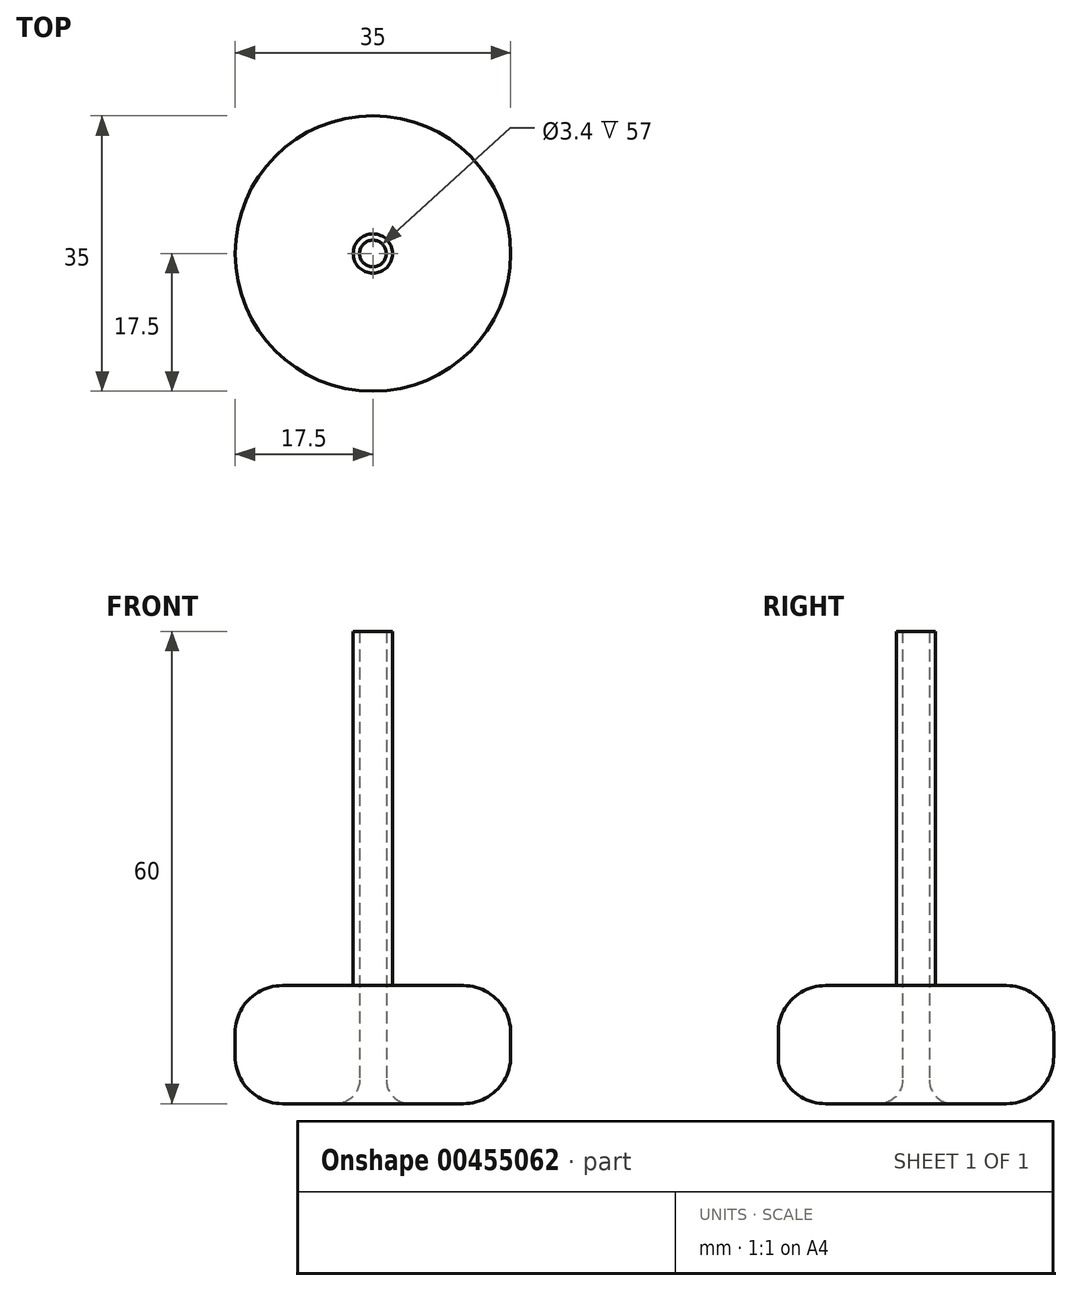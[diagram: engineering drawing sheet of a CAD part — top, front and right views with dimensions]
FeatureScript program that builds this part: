
annotation { "Feature Type Name" : "Feature", "Feature Type Description" : "" }
export const myFeature = defineFeature(function(context is Context, id is Id, definition is map)
    precondition{}
    {
        {
            var Q0;
            Q0=qCreatedBy(makeId("Top.planeOp"),FACE);
            var sketch = newSketch(context, id + "F0", { "sketchPlane" : qUnion([Q0])});
            skCircle(sketch, "E0", {"center": v(0, 0) * mm, "radius": 17.5 * mm});
            skCircle(sketch, "E1", {"center": v(0, 0) * mm, "radius": 2.5 * mm});
            skCircle(sketch, "E2", {"center": v(0, 0) * mm, "radius": 1.7 * mm});
            skSolve(sketch);
        }
        {
            var Q0;
            Q0=makeQuery(id+"F0.imprint","IMPRINT",FACE,{"disambiguationData":[TD([[makeQuery(id+"F0.imprint","IMPRINT",EDGE,{"derivedFrom":sQuery(id+"F0.wireOp",EDGE,"E0")}),1.0]])]});
            extrude(context, id + "F1", {"entities" : qUnion([Q0]), "depth" : 15 * mm});
        }
        {
            var Q0;
            Q0=makeQuery(id+"F1.opExtrude","CAP_EDGE",EDGE,{"disambiguationData":[OSD([sQuery(id+"F0.wireOp",EDGE,"E0")])],"isStart":false});
            var Q1;
            Q1=makeQuery(id+"F1.opExtrude","CAP_EDGE",EDGE,{"disambiguationData":[OSD([sQuery(id+"F0.wireOp",EDGE,"E0")])],"isStart":true});
            fillet(context, id + "F2", {"entities" : qUnion([Q0, Q1]), "radius" : 6 * mm, "tangentPropagation" : true, "allowEdgeOverflow" : false});
        }
        {
            var Q0;
            Q0=makeQuery(id+"F0.imprint","IMPRINT",FACE,{"disambiguationData":[TD([[makeQuery(id+"F0.imprint","IMPRINT",EDGE,{"derivedFrom":sQuery(id+"F0.wireOp",EDGE,"E1")}),1.0]])]});
            extrude(context, id + "F3", {"entities" : qUnion([Q0]), "operationType" : NewBodyOperationType.ADD, "depth" : 60 * mm});
        }
        {
            var Q0;
            Q0=makeQuery(id+"F3.opExtrude","CAP_EDGE",EDGE,{"disambiguationData":[OSD([sQuery(id+"F0.wireOp",EDGE,"E2")])],"isStart":true});
            var Q1;
            Q1=makeQuery(id+"F1.opExtrude","CAP_EDGE",EDGE,{"disambiguationData":[OSD([sQuery(id+"F0.wireOp",EDGE,"E1")])],"isStart":false});
            fillet(context, id + "F4", {"entities" : qUnion([Q0, Q1]), "radius" : 3 * mm, "tangentPropagation" : true, "allowEdgeOverflow" : false});
        }
    });
